# Revit family: Mixer_Sink_Abey_Builders_Squareneck_FaceBased
name_source: partatom
category: Plumbing Fixtures
units: mm (PartAtom-declared; Revit-internal decimal feet)

## family parameters
Cut with Voids When Loaded = Yes
Host = Face
Maintain Annotation Orientation = No
OmniClass Number = 23.31.11.19
OmniClass Title = Faucet Mixing Valves
Part Type = Normal
Room Calculation Point = No
Round Connector Dimension = Use Diameter
Shared = No

## types (3) — shared parameters
Assembly Code = C1030210
CW Connection = Yes
Default Elevation = 0 mm
HW Connection = Yes
IfcExportAs = IfcValve
IfcExportType = FAUCET
Manufacturer = Abey
ManufacturerOverallDepth = 250 mm
ManufacturerOverallHeight = 290 mm
ManufacturerOverallWidth = 100 mm
ManufacturerURLProductSpecific = https://www.abeyspecifier.com.au
ModifiedIssue = 20251103 $
URL = https://www.abey.com.au
Uniclass2015Code = Pr_40_20_87_55
Uniclass2015Title = Mixer taps
Uniclass2015Version = Products v1.38
Vent Connection = No
Waste Connection = No
zero-valued in all types: Cost

## per-type parameters (varying)
| type | Description | ManufacturerSpecCode | Material | Model | Type Comments |
| Chrome (4K2-LF) | Abey Builders Squareneck Kitchen Mixer Chrome | 4K2-LF | Metal_Abey_Chrome | 4K2-LF | Mixer - Sink - Squareneck - Chrome |
| Black (4K2-B-LF) | Abey Builders Squareneck Kitchen Mixer Black | 4K2-B-LF | Metal_Abey_Black | 4K2-B-LF | Mixer - Sink - Squareneck - Black |
| Brushed Nickel (4K2-BN-LF) | Abey Builders Squareneck Kitchen Mixer Brushed Nickel | 4K2-BN-LF | Metal_Abey_BrushedNickel | 4K2-BN-LF | Mixer - Sink - Squareneck - Brushed Nickel |

## geometry (parser evidence)
native form markers: Sweep x4
no freeform markers — native parametric forms only
